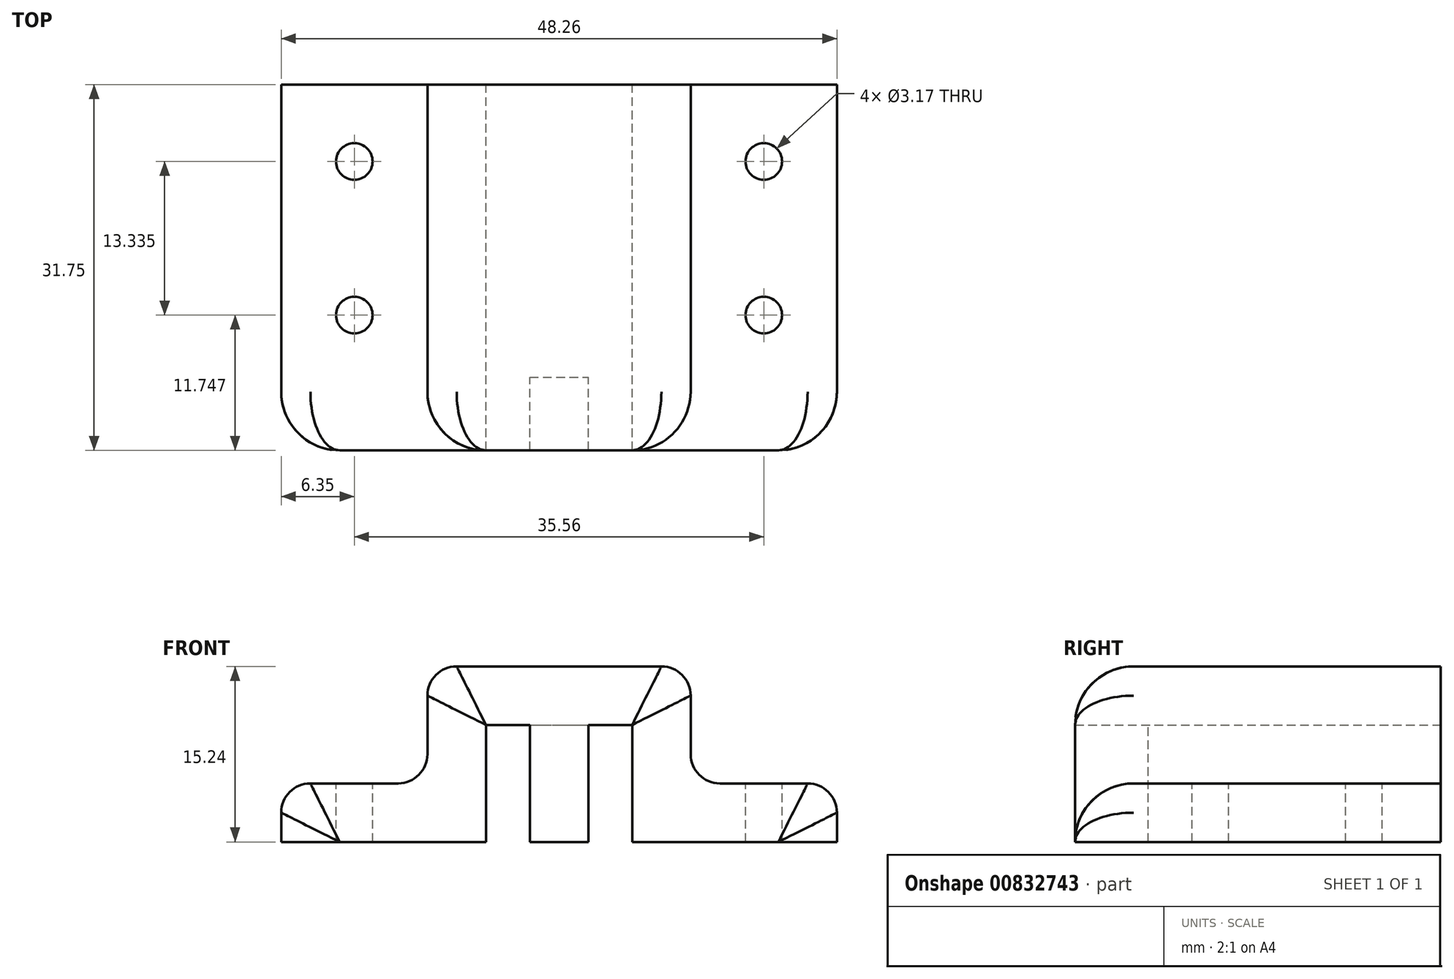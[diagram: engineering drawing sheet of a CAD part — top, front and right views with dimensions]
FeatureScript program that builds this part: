
annotation { "Feature Type Name" : "Feature", "Feature Type Description" : "" }
export const myFeature = defineFeature(function(context is Context, id is Id, definition is map)
    precondition{}
    {
        {
            var Q0;
            Q0=qCreatedBy(makeId("Front.planeOp"),FACE);
            var sketch = newSketch(context, id + "F0", { "sketchPlane" : qUnion([Q0])});
            skLineSegment(sketch, "E0", {"start": v(0, 0) * mm, "end": v(78.34, 0) * mm, "construction": true});
            skLineSegment(sketch, "E1", {"start": v(78.34, 0) * mm, "end": v(6.35, 0) * mm, "construction": true});
            skLineSegment(sketch, "E2", {"start": v(0, 0) * mm, "end": v(0, 78.64) * mm, "construction": true});
            skLineSegment(sketch, "E3", {"start": v(0, 78.64) * mm, "end": v(0, -78.46) * mm, "construction": true});
            skLineSegment(sketch, "E4.bottom", {"start": v(-6.35, 10.16) * mm, "end": v(6.35, 10.16) * mm});
            skLineSegment(sketch, "E4.left", {"start": v(-6.35, 10.16) * mm, "end": v(-6.35, 0) * mm});
            skLineSegment(sketch, "E4.right", {"start": v(6.35, 10.16) * mm, "end": v(6.35, 0) * mm});
            skLineSegment(sketch, "E5.bottom", {"start": v(-8.9, 15.24) * mm, "end": v(8.9, 15.24) * mm});
            skLineSegment(sketch, "E5.top", {"start": v(-11.43, 0) * mm, "end": v(-6.35, 0) * mm});
            skLineSegment(sketch, "E5.left", {"start": v(-11.43, 12.7) * mm, "end": v(-11.43, 7.62) * mm});
            skLineSegment(sketch, "E5.right", {"start": v(11.43, 12.7) * mm, "end": v(11.43, 7.62) * mm});
            skLineSegment(sketch, "E6.trimOffspring", {"start": v(0, 0) * mm, "end": v(-91.7, 0) * mm, "construction": true});
            skLineSegment(sketch, "E7", {"start": v(-13.97, 5.08) * mm, "end": v(-21.6, 5.08) * mm});
            skLineSegment(sketch, "E8", {"start": v(-24.13, 2.54) * mm, "end": v(-24.13, 0) * mm});
            skLineSegment(sketch, "E9", {"start": v(-24.13, 0) * mm, "end": v(-11.43, 0) * mm});
            skLineSegment(sketch, "E10", {"start": v(13.97, 5.08) * mm, "end": v(21.6, 5.08) * mm});
            skLineSegment(sketch, "E11", {"start": v(24.13, 2.54) * mm, "end": v(24.13, 0) * mm});
            skLineSegment(sketch, "E12", {"start": v(6.35, 0) * mm, "end": v(24.13, 0) * mm});
            skPoint(sketch, "E13.visualSharp", {"position": v(-11.43, 5.08) * mm});
            skArc(sketch, "E13.filletArc", {"start": v(-13.97, 5.08) * mm, "mid": v(-12.17, 5.82) * mm, "end": v(-11.43, 7.62) * mm});
            skPoint(sketch, "E14.visualSharp", {"position": v(11.43, 5.08) * mm});
            skArc(sketch, "E14.filletArc", {"start": v(11.43, 7.62) * mm, "mid": v(12.17, 5.82) * mm, "end": v(13.97, 5.08) * mm});
            skPoint(sketch, "E15.visualSharp", {"position": v(24.13, 5.08) * mm});
            skArc(sketch, "E15.filletArc", {"start": v(24.13, 2.54) * mm, "mid": v(23.39, 4.34) * mm, "end": v(21.6, 5.08) * mm});
            skPoint(sketch, "E16.visualSharp", {"position": v(-24.13, 5.08) * mm});
            skArc(sketch, "E16.filletArc", {"start": v(-21.6, 5.08) * mm, "mid": v(-23.39, 4.34) * mm, "end": v(-24.13, 2.54) * mm});
            skPoint(sketch, "E17.visualSharp", {"position": v(-11.43, 15.24) * mm});
            skArc(sketch, "E17.filletArc", {"start": v(-8.9, 15.24) * mm, "mid": v(-10.69, 14.5) * mm, "end": v(-11.43, 12.7) * mm});
            skPoint(sketch, "E18.visualSharp", {"position": v(11.43, 15.24) * mm});
            skArc(sketch, "E18.filletArc", {"start": v(11.43, 12.7) * mm, "mid": v(10.69, 14.5) * mm, "end": v(8.9, 15.24) * mm});
            skSolve(sketch);
        }
        {
            var Q0;
            Q0 = qSketchRegion(id + "F0", true);
            extrude(context, id + "F1", {"entities" : qUnion([Q0]), "depth" : 25.4 * mm, "offsetDistance" : 25.4 * mm});
        }
        {
            var Q0;
            Q0=makeQuery(id+"F1.opExtrude","CAP_FACE",FACE,{"disambiguationData":[OSD([sQuery(id+"F0.wireOp",EDGE,"E4.bottom"),sQuery(id+"F0.wireOp",EDGE,"E4.left"),sQuery(id+"F0.wireOp",EDGE,"E4.right"),sQuery(id+"F0.wireOp",EDGE,"E5.bottom"),sQuery(id+"F0.wireOp",EDGE,"E5.top"),sQuery(id+"F0.wireOp",EDGE,"E5.left"),sQuery(id+"F0.wireOp",EDGE,"E5.right"),sQuery(id+"F0.wireOp",EDGE,"E7"),sQuery(id+"F0.wireOp",EDGE,"E8"),sQuery(id+"F0.wireOp",EDGE,"E9"),sQuery(id+"F0.wireOp",EDGE,"E10"),sQuery(id+"F0.wireOp",EDGE,"E11"),sQuery(id+"F0.wireOp",EDGE,"E12"),sQuery(id+"F0.wireOp",EDGE,"E13.filletArc"),sQuery(id+"F0.wireOp",EDGE,"E14.filletArc"),sQuery(id+"F0.wireOp",EDGE,"E15.filletArc"),sQuery(id+"F0.wireOp",EDGE,"E16.filletArc"),sQuery(id+"F0.wireOp",EDGE,"E17.filletArc"),sQuery(id+"F0.wireOp",EDGE,"E18.filletArc")])],"isStart":false});
            var sketch = newSketch(context, id + "F2", { "sketchPlane" : qUnion([Q0])});
            skLineSegment(sketch, "E19", {"start": v(0, 22.94) * mm, "end": v(0, -18.66) * mm, "construction": true});
            skLineSegment(sketch, "E20.bottom", {"start": v(0, 0) * mm, "end": v(-2.54, 0) * mm});
            skLineSegment(sketch, "E20.top", {"start": v(0, 15.24) * mm, "end": v(-2.54, 15.24) * mm});
            skLineSegment(sketch, "E20.left", {"start": v(0, 0) * mm, "end": v(0, 15.24) * mm});
            skLineSegment(sketch, "E20.right", {"start": v(-2.54, 0) * mm, "end": v(-2.54, 10.16) * mm});
            skLineSegment(sketch, "E21.bottom", {"start": v(-24.13, 0) * mm, "end": v(-6.35, 0) * mm});
            skLineSegment(sketch, "E21.top", {"start": v(-21.6, 5.08) * mm, "end": v(-13.97, 5.08) * mm});
            skLineSegment(sketch, "E21.left", {"start": v(-24.13, 0) * mm, "end": v(-24.13, 2.54) * mm});
            skLineSegment(sketch, "E21.right", {"start": v(-2.54, 0) * mm, "end": v(-2.54, 5.08) * mm});
            skLineSegment(sketch, "E22", {"start": v(-2.54, 10.16) * mm, "end": v(-6.35, 10.16) * mm});
            skLineSegment(sketch, "E23", {"start": v(-6.35, 10.16) * mm, "end": v(-6.35, 0) * mm});
            skLineSegment(sketch, "E24", {"start": v(-2.54, 15.24) * mm, "end": v(-8.9, 15.24) * mm});
            skLineSegment(sketch, "E25", {"start": v(-11.43, 7.62) * mm, "end": v(-11.43, 12.7) * mm});
            skLineSegment(sketch, "E26", {"start": v(-11.43, 7.62) * mm, "end": v(-11.43, 7.62) * mm});
            skPoint(sketch, "E27.MirrorCS.end.orphan", {"position": v(2.54, 0) * mm});
            skPoint(sketch, "E27.MirrorCS.start.orphan", {"position": v(0, 0) * mm});
            skPoint(sketch, "E28.MirrorCS.end.orphan", {"position": v(2.54, 15.24) * mm});
            skPoint(sketch, "E28.MirrorCS.start.orphan", {"position": v(0, 15.24) * mm});
            skPoint(sketch, "E29.visualSharp", {"position": v(-11.43, 15.24) * mm});
            skArc(sketch, "E29.filletArc", {"start": v(-8.9, 15.24) * mm, "mid": v(-10.69, 14.5) * mm, "end": v(-11.43, 12.7) * mm});
            skPoint(sketch, "E30.visualSharp", {"position": v(-24.13, 5.08) * mm});
            skArc(sketch, "E30.filletArc", {"start": v(-21.6, 5.08) * mm, "mid": v(-23.39, 4.34) * mm, "end": v(-24.13, 2.54) * mm});
            skPoint(sketch, "E31.visualSharp", {"position": v(-11.43, 5.08) * mm});
            skArc(sketch, "E31.filletArc", {"start": v(-13.97, 5.08) * mm, "mid": v(-12.17, 5.82) * mm, "end": v(-11.43, 7.62) * mm});
            skLineSegment(sketch, "E32.MirrorCS", {"start": v(2.54, 0) * mm, "end": v(2.54, 5.08) * mm});
            skLineSegment(sketch, "E33.MirrorCS", {"start": v(0, 0) * mm, "end": v(2.54, 0) * mm});
            skLineSegment(sketch, "E34.MirrorCS", {"start": v(2.54, 0) * mm, "end": v(2.54, 10.16) * mm});
            skArc(sketch, "E35.MirrorCS", {"start": v(21.6, 5.08) * mm, "mid": v(23.39, 4.34) * mm, "end": v(24.13, 2.54) * mm});
            skArc(sketch, "E36.MirrorCS", {"start": v(8.9, 15.24) * mm, "mid": v(10.69, 14.5) * mm, "end": v(11.43, 12.7) * mm});
            skPoint(sketch, "E37.MirrorP", {"position": v(11.43, 15.24) * mm});
            skArc(sketch, "E38.MirrorCS", {"start": v(13.97, 5.08) * mm, "mid": v(12.17, 5.82) * mm, "end": v(11.43, 7.62) * mm});
            skLineSegment(sketch, "E39.MirrorCS", {"start": v(11.43, 7.62) * mm, "end": v(11.43, 7.62) * mm});
            skLineSegment(sketch, "E40.MirrorCS", {"start": v(2.54, 15.24) * mm, "end": v(8.9, 15.24) * mm});
            skPoint(sketch, "E41.MirrorP", {"position": v(24.13, 5.08) * mm});
            skPoint(sketch, "E42.MirrorP", {"position": v(11.43, 5.08) * mm});
            skLineSegment(sketch, "E43.MirrorCS", {"start": v(2.54, 10.16) * mm, "end": v(6.35, 10.16) * mm});
            skLineSegment(sketch, "E44.MirrorCS", {"start": v(24.13, 0) * mm, "end": v(24.13, 2.54) * mm});
            skLineSegment(sketch, "E45.MirrorCS", {"start": v(21.6, 5.08) * mm, "end": v(13.97, 5.08) * mm});
            skLineSegment(sketch, "E46.MirrorCS", {"start": v(0, 15.24) * mm, "end": v(2.54, 15.24) * mm});
            skLineSegment(sketch, "E47.MirrorCS", {"start": v(24.13, 0) * mm, "end": v(6.35, 0) * mm});
            skLineSegment(sketch, "E48.MirrorCS", {"start": v(6.35, 10.16) * mm, "end": v(6.35, 0) * mm});
            skLineSegment(sketch, "E49.MirrorCS", {"start": v(11.43, 7.62) * mm, "end": v(11.43, 12.7) * mm});
            skSolve(sketch);
        }
        {
            var Q0;
            Q0 = qSketchRegion(id + "F2", true);
            extrude(context, id + "F3", {"entities" : qUnion([Q0]), "operationType" : NewBodyOperationType.ADD, "depth" : 6.35 * mm, "offsetDistance" : 25.4 * mm});
        }
        {
            var Q0;
            Q0=makeQuery(id+"F3.opExtrude","CAP_EDGE",EDGE,{"disambiguationData":[OSD([sQuery(id+"F2.wireOp",EDGE,"E20.top"),sQuery(id+"F2.wireOp",EDGE,"E24"),sQuery(id+"F2.wireOp",EDGE,"E40.MirrorCS"),sQuery(id+"F2.wireOp",EDGE,"E46.MirrorCS")])],"isStart":false});
            fillet(context, id + "F4", {"entities" : qUnion([Q0]), "radius" : 5.08 * mm, "tangentPropagation" : true, "allowEdgeOverflow" : false});
        }
        {
            var Q0;
            Q0=makeQuery(id+"F3.boolean.opBoolean","MERGE",FACE,{"derivedFrom":[makeQuery(id+"F1.opExtrude","SWEPT_FACE",FACE,{"disambiguationData":[OSD([sQuery(id+"F0.wireOp",EDGE,"E10")])]}),makeQuery(id+"F3.opExtrude","SWEPT_FACE",FACE,{"disambiguationData":[OSD([sQuery(id+"F2.wireOp",EDGE,"E45.MirrorCS")])]})]});
            var sketch = newSketch(context, id + "F5", { "sketchPlane" : qUnion([Q0])});
            skLineSegment(sketch, "E50", {"start": v(17.78, 0) * mm, "end": v(17.78, -26.67) * mm, "construction": true});
            skLineSegment(sketch, "E51", {"start": v(21.6, -13.34) * mm, "end": v(-28.1, -13.34) * mm, "construction": true});
            skLineSegment(sketch, "E52", {"start": v(17.78, -6.67) * mm, "end": v(-28.1, -6.67) * mm, "construction": true});
            skLineSegment(sketch, "E53.MirrorCS", {"start": v(17.78, -20) * mm, "end": v(-28.1, -20) * mm, "construction": true});
            skCircle(sketch, "E54", {"center": v(17.78, -6.67) * mm, "radius": 1.59 * mm});
            skCircle(sketch, "E55.MirrorC", {"center": v(17.78, -20) * mm, "radius": 1.59 * mm});
            skCircle(sketch, "E56.MirrorC", {"center": v(-17.78, -6.67) * mm, "radius": 1.59 * mm});
            skCircle(sketch, "E57.MirrorC", {"center": v(-17.78, -20) * mm, "radius": 1.59 * mm});
            skSolve(sketch);
        }
        {
            var Q0;
            Q0 = qSketchRegion(id + "F5", true);
            extrude(context, id + "F6", {"entities" : qUnion([Q0]), "operationType" : NewBodyOperationType.REMOVE, "endBound" : BoundingType.THROUGH_ALL, "oppositeDirection" : true, "depth" : 25.4 * mm, "offsetDistance" : 25.4 * mm});
        }
    });
